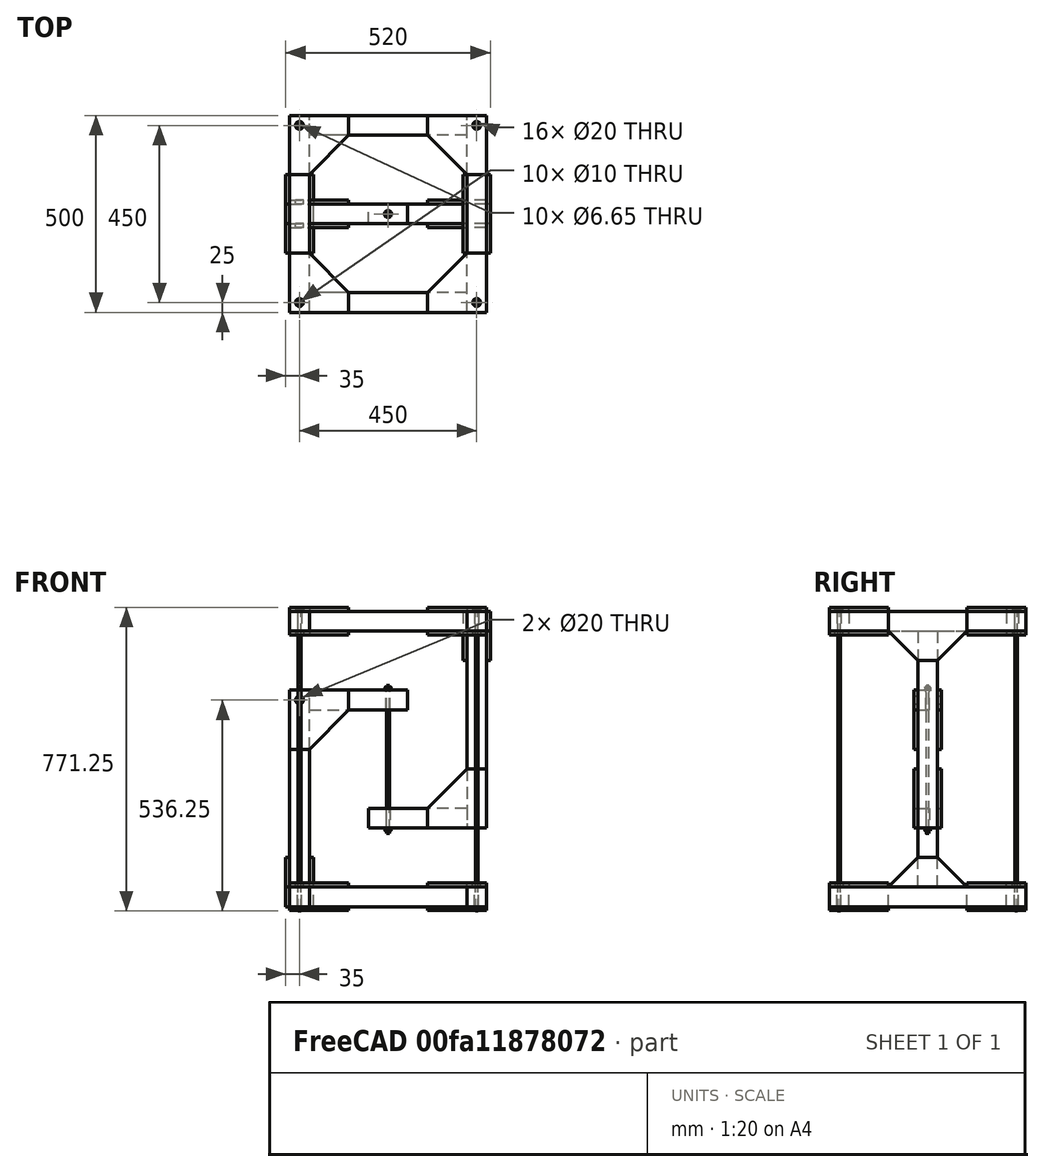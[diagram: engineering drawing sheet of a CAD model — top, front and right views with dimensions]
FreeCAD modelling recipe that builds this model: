
FCSTD DOCUMENT  (FreeCAD 0.19R23721 (Git))
Label: TENSEGRITY STRUCTURE
License: All rights reserved
LicenseURL: http://en.wikipedia.org/wiki/All_rights_reserved
objects: Part::Feature×13, Part::Box×6, Part::Compound×6, Part::FeaturePython×6, Part::Cylinder×3, Part::Cut×3, Part::Chamfer×2
note: 39 computed .brp shape members not serialized (recipe doc carries the construction recipe); baked Part::Feature solids carry a one-line shape summary decoded from their .brp

FEATURE [Part::Box] Box  label="Cube"
  AttacherType = Attacher::AttachEngine3D
  Height = 50
  Length = 50
  Placement = pos=(-250,-250,-25) rot=(0,0,1;0rad)
  Width = 500
FEATURE [Part::Cylinder] Cylinder
  Angle = 360
  AttacherType = Attacher::AttachEngine3D
  Height = 50
  Placement = pos=(-225,-225,-25) rot=(0,0,1;0rad)
  Radius = 5
FEATURE [Part::Feature] Cylinder001
  Placement = pos=(-225,225,-25) rot=(0,0,1;0rad)
  shape: bbox 10 x 10 x 50 mm, 3 faces (baked)
FEATURE [Part::Compound] Compound
  Links = -> [Cylinder001,Cylinder]
FEATURE [Part::Cut] Cut
  Base = -> Box
  Tool = -> Compound
FEATURE [Part::Box] Box001  label="Cube001"
  AttacherType = Attacher::AttachEngine3D
  Height = 50
  Length = 400
  Placement = pos=(-200,-250,-25) rot=(0,0,1;0rad)
  Width = 50
FEATURE [Part::Feature] Box001001  label="Cube002"
  Placement = pos=(-200,200,-25) rot=(0,0,1;0rad)
  shape: bbox 400 x 50 x 50 mm, 6 faces (baked)
FEATURE [Part::Feature] Cut001
  Placement = pos=(450,0,0) rot=(0,0,1;0rad)
  shape: bbox 50 x 500 x 50 mm, 8 faces (baked)
FEATURE [Part::Box] Box001002  label="Cube003"
  AttacherType = Attacher::AttachEngine3D
  Height = 500
  Length = 50
  Placement = pos=(-250,-25,25) rot=(0,0,1;0rad)
  Width = 50
FEATURE [Part::Box] Box001003  label="Cube004"
  AttacherType = Attacher::AttachEngine3D
  Height = 50
  Length = 250
  Placement = pos=(-200,-25,475) rot=(0,0,1;0rad)
  Width = 50
FEATURE [Part::Cylinder] Cylinder002
  Angle = 360
  AttacherType = Attacher::AttachEngine3D
  Height = 50
  Placement = pos=(0,0,475) rot=(0,0,1;0rad)
  Radius = 5
FEATURE [Part::Cut] Cut002
  Base = -> Box001003
  Tool = -> Cylinder002
FEATURE [Part::Box] Box001004  label="Cube005"
  AttacherType = Attacher::AttachEngine3D
  Height = 10
  Length = 150
  Width = 150
FEATURE [Part::Chamfer] Chamfer
  Base = -> Box001004
  Edges = 1 edges r=100: [Edge7]
FEATURE [Part::Cylinder] Cylinder003
  Angle = 360
  AttacherType = Attacher::AttachEngine3D
  Height = 10
  Placement = pos=(25,25,0) rot=(0,0,1;0rad)
  Radius = 10
FEATURE [Part::Cut] Cut003
  Base = -> Chamfer
  Placement = pos=(-250,-250,25) rot=(0,0,1;0rad)
  Tool = -> Cylinder003
FEATURE [Part::Feature] Cut003001
  Placement = pos=(-250,-250,-35) rot=(0,0,1;0rad)
  shape: bbox 150 x 150 x 10 mm, 8 faces (baked)
FEATURE [Part::Compound] Compound001
  Links = -> [Cut003001,Cut003]
FEATURE [Part::Feature] Compound001001
  Placement = pos=(0,0,0) rot=(1,0,0;3.14159rad)
  shape: bbox 150 x 150 x 70 mm, 16 faces, 2 solids (baked)
FEATURE [Part::Compound] Compound001002
  Links = -> [Compound001,Compound001001]
FEATURE [Part::Feature] Compound001002001
  Placement = pos=(0,0,0) rot=(0,0,1;3.14159rad)
  shape: bbox 150 x 500 x 70 mm, 32 faces, 4 solids (baked)
FEATURE [Part::Feature] Compound001002002
  Placement = pos=(0,6.11e-14,275) rot=(1,0,0;4.71239rad)
  shape: bbox 150 x 70 x 150 mm, 16 faces, 2 solids (baked)
FEATURE [Part::Feature] Defeatured
  shape: bbox 150 x 70 x 150 mm, 14 faces, 2 solids (baked)
FEATURE [Part::Box] Box001005  label="Cube006"
  AttacherType = Attacher::AttachEngine3D
  Height = 125
  Length = 10
  Width = 200
FEATURE [Part::Chamfer] Chamfer001
  Base = -> Box001005
  Edges = 2 edges r=75: [Edge10,Edge12]
  Placement = pos=(-200,-100,-25) rot=(0,0,1;0rad)
FEATURE [Part::Feature] Chamfer001001
  Placement = pos=(-260,-100,-25) rot=(0,0,1;0rad)
  shape: bbox 10 x 200 x 125 mm, 8 faces (baked)
FEATURE [Part::Compound] Compound001002003
  Links = -> [Chamfer001001,Chamfer001,Defeatured,Compound001002001,Compound001002,Cut002,Box001002,Cut001,Box001001,Box001,Cut]
FEATURE [Part::Feature] Compound001002003001
  Placement = pos=(0,-8.57e-14,700) rot=(0,1,0;3.14159rad)
  shape: bbox 510 x 500 x 560 mm, 135 faces, 18 solids (baked)
FEATURE [Part::FeaturePython] Nut  label="M8-Nut"  # Fasteners workbench fastener (typed FeaturePython)
  Placement = pos=(0,0,525) rot=(0,0,1;0rad)
  baseObject = -> Compound001002003 [Edge220]
  diameter = 3
  invert = false
  matchOuter = false
  offset = 0
  thread = false
  type = 3
FEATURE [Part::FeaturePython] Nut001  label="M8-Nut001"  # Fasteners workbench fastener (typed FeaturePython)
  Placement = pos=(0,-2.14e-14,175) rot=(-1,0,0;3.14159rad)
  baseObject = -> Compound001002003001 [Edge220]
  diameter = 3
  invert = false
  matchOuter = false
  offset = 0
  thread = false
  type = 3
FEATURE [Part::FeaturePython] ScrewTap  label="M8x375.0-ScrewTap"  # Fasteners workbench fastener (typed FeaturePython)
  Placement = pos=(0,-1.98e-14,162) rot=(-1,0,0;3.14159rad)
  baseObject = -> Nut001 [Edge1]
  diameter = 9
  invert = false
  length = 375
  matchOuter = false
  offset = 5
  thread = false
FEATURE [Part::Compound] Compound001002003002
  Links = -> [ScrewTap,Nut001,Nut]
FEATURE [Part::FeaturePython] Nut002  label="M8-Nut002"  # Fasteners workbench fastener (typed FeaturePython)
  Placement = pos=(-225,-225,-25) rot=(-1,0,0;3.14159rad)
  baseObject = -> Compound001002003 [Edge294]
  diameter = 3
  invert = true
  matchOuter = false
  offset = 0
  thread = false
  type = 3
FEATURE [Part::FeaturePython] Nut003  label="M8-Nut003"  # Fasteners workbench fastener (typed FeaturePython)
  Placement = pos=(-225,-225,725) rot=(0,0,1;0rad)
  baseObject = -> Compound001002003001 [Edge252]
  diameter = 3
  invert = true
  matchOuter = false
  offset = 0
  thread = false
  type = 3
FEATURE [Part::FeaturePython] ScrewTap001  label="M8x770.0-ScrewTap"  # Fasteners workbench fastener (typed FeaturePython)
  Placement = pos=(-225,-225,-35) rot=(-1,0,0;3.14159rad)
  baseObject = -> Nut002 [Edge1]
  diameter = 9
  invert = false
  length = 770
  matchOuter = false
  offset = 2
  thread = false
FEATURE [Part::Compound] Compound001002003003
  Links = -> [ScrewTap001,Nut003,Nut002]
FEATURE [Part::Feature] Compound001002003003001
  Placement = pos=(450,0,0) rot=(0,0,1;0rad)
  shape: bbox 17.9 x 17.9 x 771.3 mm, 43 faces, 3 solids (baked)
FEATURE [Part::Feature] Compound001002003003001001
  Placement = pos=(450,450,0) rot=(0,0,1;0rad)
  shape: bbox 17.9 x 17.9 x 771.3 mm, 43 faces, 3 solids (baked)
FEATURE [Part::Feature] Compound001002003003001001001
  Placement = pos=(0,450,0) rot=(0,0,1;0rad)
  shape: bbox 17.9 x 17.9 x 771.3 mm, 43 faces, 3 solids (baked)
